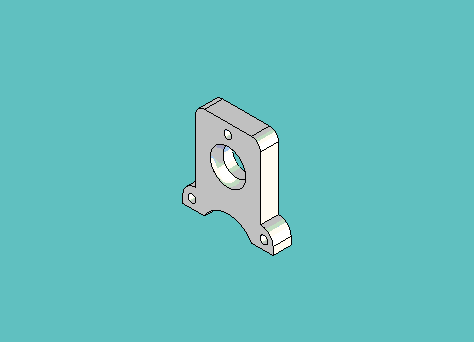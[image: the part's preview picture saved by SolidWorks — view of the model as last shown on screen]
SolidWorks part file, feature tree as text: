
SOLIDWORKS PART (.sldprt)
format: sldprt  version: not decoded by parser v0  size: 536,576 bytes
history: native  units: mm
features: sketch x4, cut_extrude x2, material x1, extrude x1, revolve x1, boolean_combine x1 (+11 scaffold rows collapsed)
feature tree (21):
  scaffold x11  (default folders/planes/origin — collapsed)
  material  "Material <not specified>"
  sketch  "Sketch1"  dims[c1.D1=7.9375mm c1.D4=9.525mm c1.D7=3.175mm c1.D8=4.445mm c1.D2=14.732mm c1.D3=33.3375mm c2.D1=11.43mm c2.D2=~25.17775mm c2.D3=12.1285mm c2.D5=7.366mm c2.D6=15.875mm c2.D9=~4.66725mm c3.D2=0.0mm]
  extrude  "Extrude1"  Depth=6.35mm
  sketch  "Sketch2"  dims[c1.D1=~2.778125mm c1.D2=~2.778125mm c1.D3=~2.778125mm c1.D4=4.191mm c1.D5=12.7mm c2.D2=21.5265mm]
  sketch  "Sketch3"  dims[c1.D3=12.7mm c1.D1=14.2875mm c1.D2=11.684mm c2.D1=~1.190625mm]
  revolve  "Revolve1"  Angle=360deg
  boolean_combine  "Combine1"
  sketch  "Sketch4"  dims[D1=9.525mm]
  cut_extrude  "Cut-Extrude2"  [1 undecoded]
  cut_extrude  "Cut-Extrude1"  [1 undecoded]
decode coverage: 6 of 9 modeling features carry decoded parameters
note: ~ marks probable driven/reference dimensions
note: 2 parameter values undecoded
note: suppression state not decoded; provenance and decode notes live in map.json
